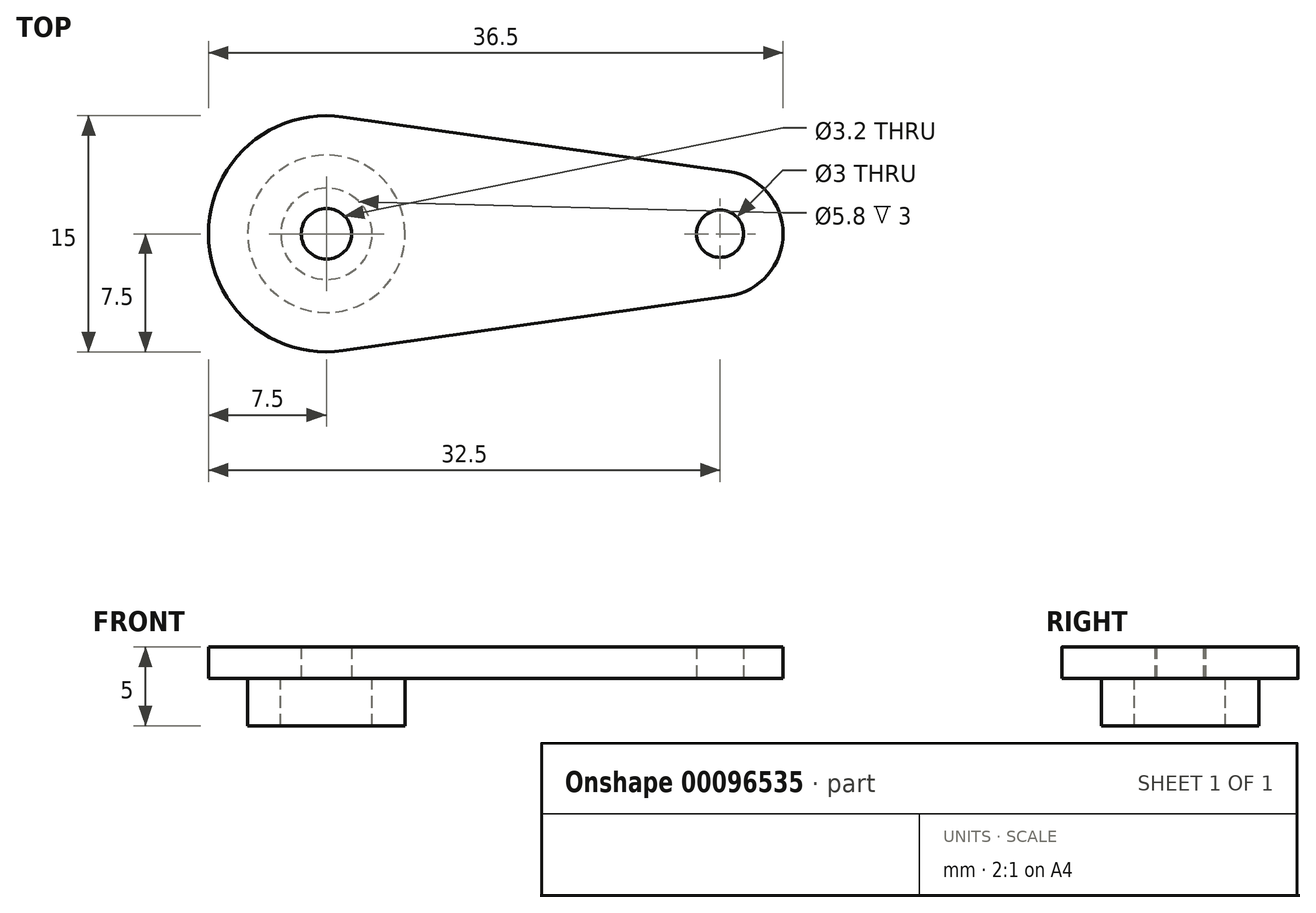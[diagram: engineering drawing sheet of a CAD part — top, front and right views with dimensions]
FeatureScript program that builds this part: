
annotation { "Feature Type Name" : "Feature", "Feature Type Description" : "" }
export const myFeature = defineFeature(function(context is Context, id is Id, definition is map)
    precondition{}
    {
        {
            var Q0;
            Q0=qCreatedBy(makeId("Top.planeOp"),FACE);
            var sketch = newSketch(context, id + "F0", { "sketchPlane" : qUnion([Q0])});
            skArc(sketch, "E0", {"start": v(1.05, 7.43) * mm, "mid": v(-7.5, 0) * mm, "end": v(1.05, -7.43) * mm});
            skArc(sketch, "E1", {"start": v(25.56, -3.96) * mm, "mid": v(29, 0) * mm, "end": v(25.56, 3.96) * mm});
            skLineSegment(sketch, "E2", {"start": v(1.05, 7.43) * mm, "end": v(25.56, 3.96) * mm});
            skLineSegment(sketch, "E3", {"start": v(1.05, -7.43) * mm, "end": v(25.56, -3.96) * mm});
            skCircle(sketch, "E4", {"center": v(0, 0) * mm, "radius": 1.6 * mm});
            skCircle(sketch, "E5", {"center": v(25, 0) * mm, "radius": 1.5 * mm});
            skSolve(sketch);
        }
        {
            var Q0;
            Q0 = qSketchRegion(id + "F0", true);
            extrude(context, id + "F1", {"entities" : qUnion([Q0]), "depth" : 2 * mm});
        }
        {
            var Q0;
            Q0=makeQuery(id+"F1.opExtrude","CAP_FACE",FACE,{"disambiguationData":[OSD([sQuery(id+"F0.wireOp",EDGE,"E0"),sQuery(id+"F0.wireOp",EDGE,"E1"),sQuery(id+"F0.wireOp",EDGE,"E2"),sQuery(id+"F0.wireOp",EDGE,"E3"),sQuery(id+"F0.wireOp",EDGE,"E4"),sQuery(id+"F0.wireOp",EDGE,"E5")])],"isStart":true});
            var sketch = newSketch(context, id + "F2", { "sketchPlane" : qUnion([Q0])});
            skCircle(sketch, "E6", {"center": v(0, 0) * mm, "radius": 5 * mm});
            skCircle(sketch, "E7", {"center": v(0, 0) * mm, "radius": 2.9 * mm});
            skSolve(sketch);
        }
        {
            var Q0;
            Q0 = qSketchRegion(id + "F2", true);
            extrude(context, id + "F3", {"entities" : qUnion([Q0]), "operationType" : NewBodyOperationType.ADD, "depth" : 3 * mm});
        }
    });
